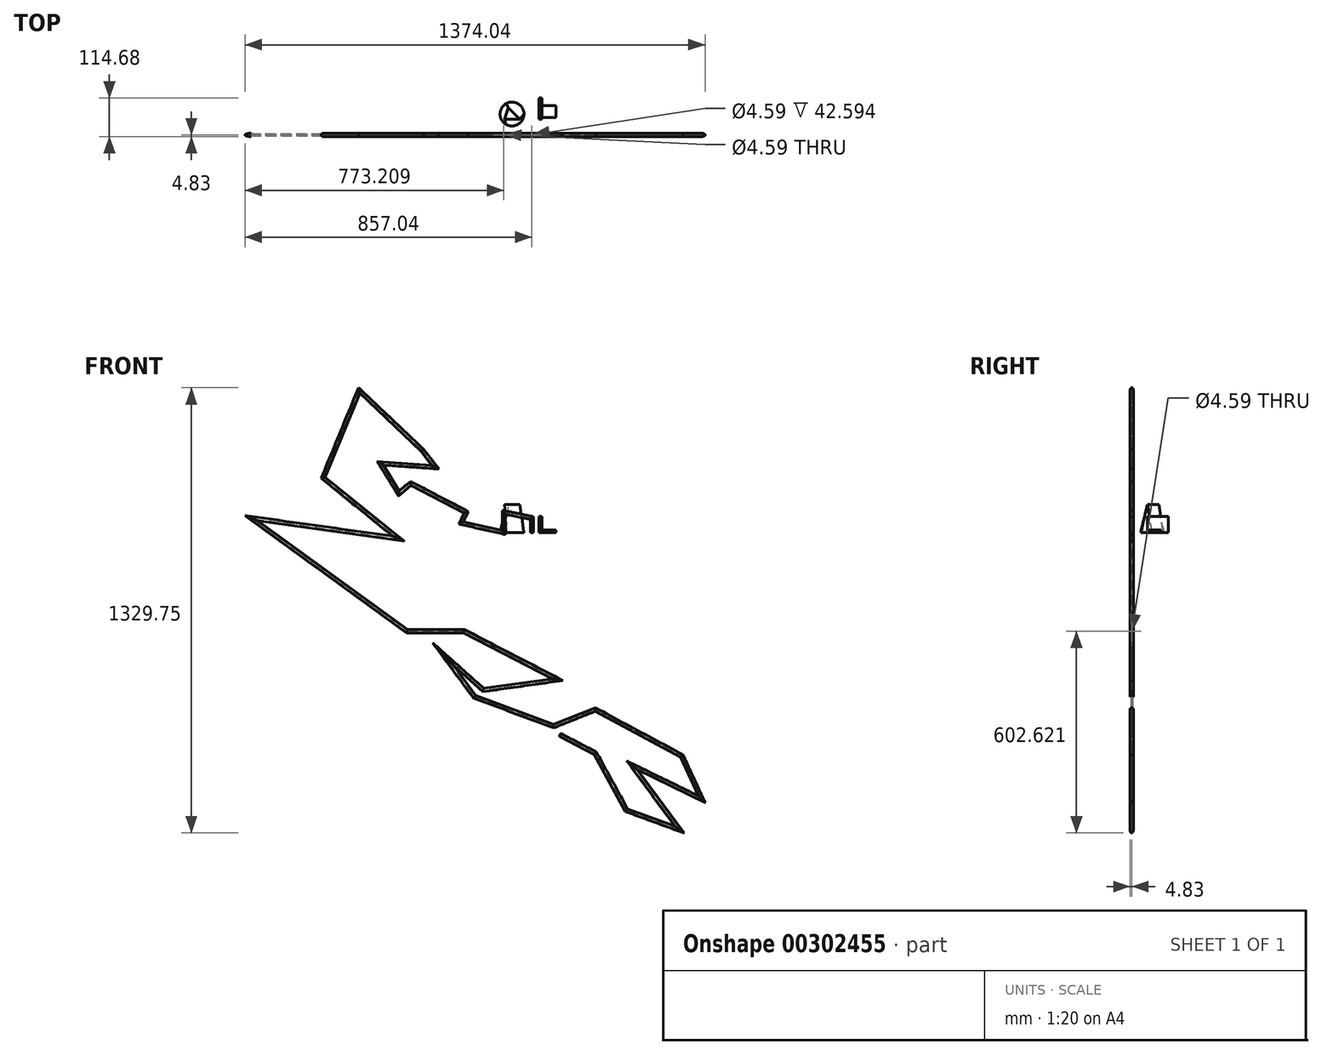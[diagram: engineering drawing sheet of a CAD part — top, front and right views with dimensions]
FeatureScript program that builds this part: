
annotation { "Feature Type Name" : "Feature", "Feature Type Description" : "" }
export const myFeature = defineFeature(function(context is Context, id is Id, definition is map)
    precondition{}
    {
        {
            var Q0;
            Q0=qCreatedBy(makeId("Top.planeOp"),FACE);
            var sketch = newSketch(context, id + "F0", { "sketchPlane" : qUnion([Q0])});
            skCircle(sketch, "E0", {"center": v(0, 0) * mm, "radius": 4.83 * mm});
            skSolve(sketch);
        }
        {
            var Q0;
            Q0=qCreatedBy(makeId("Front.planeOp"),FACE);
            var sketch = newSketch(context, id + "F1", { "sketchPlane" : qUnion([Q0])});
            skLineSegment(sketch, "E1", {"start": v(0, 0) * mm, "end": v(0, 43.26) * mm});
            skLineSegment(sketch, "E2", {"start": v(0, 43.26) * mm, "end": v(-83.83, 60.52) * mm});
            skLineSegment(sketch, "E3", {"start": v(-83.83, 60.52) * mm, "end": v(-83.83, 0) * mm});
            skLineSegment(sketch, "E4", {"start": v(-83.83, 0) * mm, "end": v(-211.39, 28.63) * mm});
            skLineSegment(sketch, "E5", {"start": v(-211.39, 28.63) * mm, "end": v(-196.26, 60.52) * mm});
            skLineSegment(sketch, "E6", {"start": v(-196.26, 60.52) * mm, "end": v(-361.95, 146.81) * mm});
            skLineSegment(sketch, "E7", {"start": v(-361.95, 146.81) * mm, "end": v(-397.46, 116.73) * mm});
            skLineSegment(sketch, "E8", {"start": v(-397.46, 116.73) * mm, "end": v(-453.35, 206.93) * mm});
            skLineSegment(sketch, "E9", {"start": v(-453.35, 206.93) * mm, "end": v(-288.31, 195.4) * mm});
            skLineSegment(sketch, "E10", {"start": v(-288.31, 195.4) * mm, "end": v(-327.1, 245.55) * mm});
            skLineSegment(sketch, "E11", {"start": v(-327.1, 245.55) * mm, "end": v(-515.9, 424.1) * mm});
            skLineSegment(sketch, "E12", {"start": v(-515.9, 424.1) * mm, "end": v(-623.44, 163.3) * mm});
            skLineSegment(sketch, "E13", {"start": v(-623.44, 163.3) * mm, "end": v(-398.8, -18) * mm});
            skLineSegment(sketch, "E14", {"start": v(-398.8, -18) * mm, "end": v(-838.51, 43.26) * mm});
            skLineSegment(sketch, "E15", {"start": v(-838.51, 43.26) * mm, "end": v(-372.51, -294.68) * mm});
            skLineSegment(sketch, "E16", {"start": v(-372.51, -294.68) * mm, "end": v(-202.84, -294.68) * mm});
            skLineSegment(sketch, "E17", {"start": v(-202.84, -294.68) * mm, "end": v(76.76, -439.3) * mm});
            skLineSegment(sketch, "E18", {"start": v(76.76, -439.3) * mm, "end": v(-145.48, -470.28) * mm});
            skLineSegment(sketch, "E19", {"start": v(-145.48, -470.28) * mm, "end": v(-264.97, -363.63) * mm});
            skLineSegment(sketch, "E20", {"start": v(-264.97, -363.63) * mm, "end": v(-171.77, -490.25) * mm});
            skLineSegment(sketch, "E21", {"start": v(-171.77, -490.25) * mm, "end": v(64.81, -578.19) * mm});
            skLineSegment(sketch, "E22", {"start": v(64.81, -578.19) * mm, "end": v(189.08, -528.56) * mm});
            skLineSegment(sketch, "E23", {"start": v(189.08, -528.56) * mm, "end": v(447.18, -667.27) * mm});
            skLineSegment(sketch, "E24", {"start": v(447.18, -667.27) * mm, "end": v(506.92, -796.48) * mm});
            skLineSegment(sketch, "E25", {"start": v(506.92, -796.48) * mm, "end": v(299.01, -695.29) * mm});
            skLineSegment(sketch, "E26", {"start": v(299.01, -695.29) * mm, "end": v(440, -887.2) * mm});
            skLineSegment(sketch, "E27", {"start": v(440, -887.2) * mm, "end": v(282.28, -829.04) * mm});
            skLineSegment(sketch, "E28", {"start": v(282.28, -829.04) * mm, "end": v(189.08, -659.08) * mm});
            skLineSegment(sketch, "E29", {"start": v(189.08, -659.08) * mm, "end": v(83.93, -604.3) * mm});
            skSolve(sketch);
        }
        {
            var Q0;
            Q0=makeQuery(id+"F0.imprint","IMPRINT",FACE,{"disambiguationData":[TD([[makeQuery(id+"F0.imprint","IMPRINT",EDGE,{"derivedFrom":sQuery(id+"F0.wireOp",EDGE,"E0")}),1.0]])]});
            var Q1;
            Q1=sQuery(id+"F1.wireOp",EDGE,"E2");
            var Q2;
            Q2=sQuery(id+"F1.wireOp",EDGE,"E1");
            var Q3;
            Q3=sQuery(id+"F1.wireOp",EDGE,"E3");
            var Q4;
            Q4=sQuery(id+"F1.wireOp",EDGE,"E4");
            var Q5;
            Q5=sQuery(id+"F1.wireOp",EDGE,"E5");
            var Q6;
            Q6=sQuery(id+"F1.wireOp",EDGE,"E6");
            var Q7;
            Q7=sQuery(id+"F1.wireOp",EDGE,"E7");
            var Q8;
            Q8=sQuery(id+"F1.wireOp",EDGE,"E9");
            var Q9;
            Q9=sQuery(id+"F1.wireOp",EDGE,"E8");
            var Q10;
            Q10=sQuery(id+"F1.wireOp",EDGE,"E10");
            var Q11;
            Q11=sQuery(id+"F1.wireOp",EDGE,"E11");
            var Q12;
            Q12=sQuery(id+"F1.wireOp",EDGE,"E12");
            var Q13;
            Q13=sQuery(id+"F1.wireOp",EDGE,"E13");
            var Q14;
            Q14=sQuery(id+"F1.wireOp",EDGE,"E14");
            var Q15;
            Q15=sQuery(id+"F1.wireOp",EDGE,"E15");
            var Q16;
            Q16=sQuery(id+"F1.wireOp",EDGE,"E16");
            var Q17;
            Q17=sQuery(id+"F1.wireOp",EDGE,"E17");
            var Q18;
            Q18=sQuery(id+"F1.wireOp",EDGE,"E18");
            var Q19;
            Q19=sQuery(id+"F1.wireOp",EDGE,"E19");
            var Q20;
            Q20=sQuery(id+"F1.wireOp",EDGE,"E20");
            var Q21;
            Q21=sQuery(id+"F1.wireOp",EDGE,"E21");
            var Q22;
            Q22=sQuery(id+"F1.wireOp",EDGE,"E22");
            var Q23;
            Q23=sQuery(id+"F1.wireOp",EDGE,"E23");
            var Q24;
            Q24=sQuery(id+"F1.wireOp",EDGE,"E24");
            var Q25;
            Q25=sQuery(id+"F1.wireOp",EDGE,"E25");
            var Q26;
            Q26=sQuery(id+"F1.wireOp",EDGE,"E26");
            var Q27;
            Q27=sQuery(id+"F1.wireOp",EDGE,"E27");
            var Q28;
            Q28=sQuery(id+"F1.wireOp",EDGE,"E28");
            var Q29;
            Q29=sQuery(id+"F1.wireOp",EDGE,"E29");
            sweep(context, id + "F2", {"profiles" : qUnion([Q0]), "path" : qUnion([Q1, Q2, Q3, Q4, Q5, Q6, Q7, Q8, Q9, Q10, Q11, Q12, Q13, Q14, Q15, Q16, Q17, Q18, Q19, Q20, Q21, Q22, Q23, Q24, Q25, Q26, Q27, Q28, Q29])});
        }
        {
            var Q0;
            Q0=qCreatedBy(makeId("Top.planeOp"),FACE);
            var sketch = newSketch(context, id + "F3", { "sketchPlane" : qUnion([Q0])});
            skCircle(sketch, "E30", {"center": v(-59.56, 62.6) * mm, "radius": 35.77 * mm});
            skSolve(sketch);
        }
        {
            var Q0;
            Q0=qCreatedBy(makeId("Top.planeOp"),FACE);
            cPlane(context, id + "F4", {"entities" : qUnion([Q0]), "cplaneType" : CPlaneType.OFFSET, "offset" : 83.31 * mm, "width" : 152.4 * mm, "height" : 152.4 * mm});
        }
        {
            var Q0;
            Q0=qCreatedBy(id+"F4.planeOp",FACE);
            var sketch = newSketch(context, id + "F5", { "sketchPlane" : qUnion([Q0])});
            skLineSegment(sketch, "E31", {"start": v(-69.88, 81.08) * mm, "end": v(-81.55, 47.05) * mm});
            skLineSegment(sketch, "E32", {"start": v(-81.55, 47.05) * mm, "end": v(-35.86, 47.05) * mm});
            skLineSegment(sketch, "E33", {"start": v(-35.86, 47.05) * mm, "end": v(-69.88, 81.08) * mm});
            skSolve(sketch);
        }
        {
            var Q0;
            Q0=makeQuery(id+"F3.imprint","IMPRINT",FACE,{"disambiguationData":[TD([[makeQuery(id+"F3.imprint","IMPRINT",EDGE,{"derivedFrom":sQuery(id+"F3.wireOp",EDGE,"E30")}),1.0]])]});
            var Q1;
            Q1=makeQuery(id+"F5.imprint","IMPRINT",FACE,{"disambiguationData":[TD([[makeQuery(id+"F5.imprint","IMPRINT",EDGE,{"derivedFrom":sQuery(id+"F5.wireOp",EDGE,"E31")}),1.0]])]});
            loft(context, id + "F6", {"sheetProfilesArray" : [{ "sheetProfileEntities" : qUnion([Q0]) }, { "sheetProfileEntities" : qUnion([Q1]) }]});
        }
        {
            var Q0;
            Q0=makeQuery(id+"F2.opSweep","CAP_FACE",FACE,{"disambiguationData":[OSD([sQuery(id+"F0.wireOp",EDGE,"E0"),sQuery(id+"F1.wireOp",VERTEX,"E29.end")])],"isStart":false});
            shell(context, id + "F7", {"entities" : qUnion([Q0]), "thickness" : 2.54 * mm});
        }
        {
            var Q0;
            Q0=qCreatedBy(makeId("Top.planeOp"),FACE);
            var sketch = newSketch(context, id + "F8", { "sketchPlane" : qUnion([Q0])});
            skLineSegment(sketch, "E34.bottom", {"start": v(71.31, 51.85) * mm, "end": v(29.32, 51.85) * mm});
            skLineSegment(sketch, "E34.top", {"start": v(71.31, 87.98) * mm, "end": v(29.32, 87.98) * mm});
            skLineSegment(sketch, "E34.left", {"start": v(71.31, 51.85) * mm, "end": v(71.31, 87.98) * mm});
            skLineSegment(sketch, "E34.right", {"start": v(29.32, 51.85) * mm, "end": v(29.32, 87.98) * mm});
            skSolve(sketch);
        }
        {
            var Q0;
            Q0=makeQuery(id+"F8.imprint","IMPRINT",FACE,{"disambiguationData":[TD([[makeQuery(id+"F8.imprint","IMPRINT",EDGE,{"derivedFrom":sQuery(id+"F8.wireOp",EDGE,"E34.bottom")}),-1.0]])]});
            extrude(context, id + "F9", {"entities" : qUnion([Q0]), "depth" : 7.62 * mm});
        }
        {
            var Q0;
            Q0=makeQuery(id+"F9.opExtrude","SWEPT_FACE",FACE,{"disambiguationData":[OSD([sQuery(id+"F8.wireOp",EDGE,"E34.right")])]});
            var sketch = newSketch(context, id + "F10", { "sketchPlane" : qUnion([Q0])});
            skLineSegment(sketch, "E35.bottom", {"start": v(-109.85, 48.62) * mm, "end": v(-47.54, 48.62) * mm});
            skLineSegment(sketch, "E35.top", {"start": v(-109.85, 0) * mm, "end": v(-47.54, 0) * mm});
            skLineSegment(sketch, "E35.left", {"start": v(-109.85, 48.62) * mm, "end": v(-109.85, 0) * mm});
            skLineSegment(sketch, "E35.right", {"start": v(-47.54, 48.62) * mm, "end": v(-47.54, 0) * mm});
            skSolve(sketch);
        }
        {
            var Q0;
            Q0=makeQuery(id+"F10.imprint","IMPRINT",FACE,{"disambiguationData":[TD([[makeQuery(id+"F10.imprint","IMPRINT",EDGE,{"derivedFrom":sQuery(id+"F10.wireOp",EDGE,"E35.bottom")}),-1.0]])]});
            extrude(context, id + "F11", {"entities" : qUnion([Q0]), "depth" : 7.87 * mm});
        }
    });
